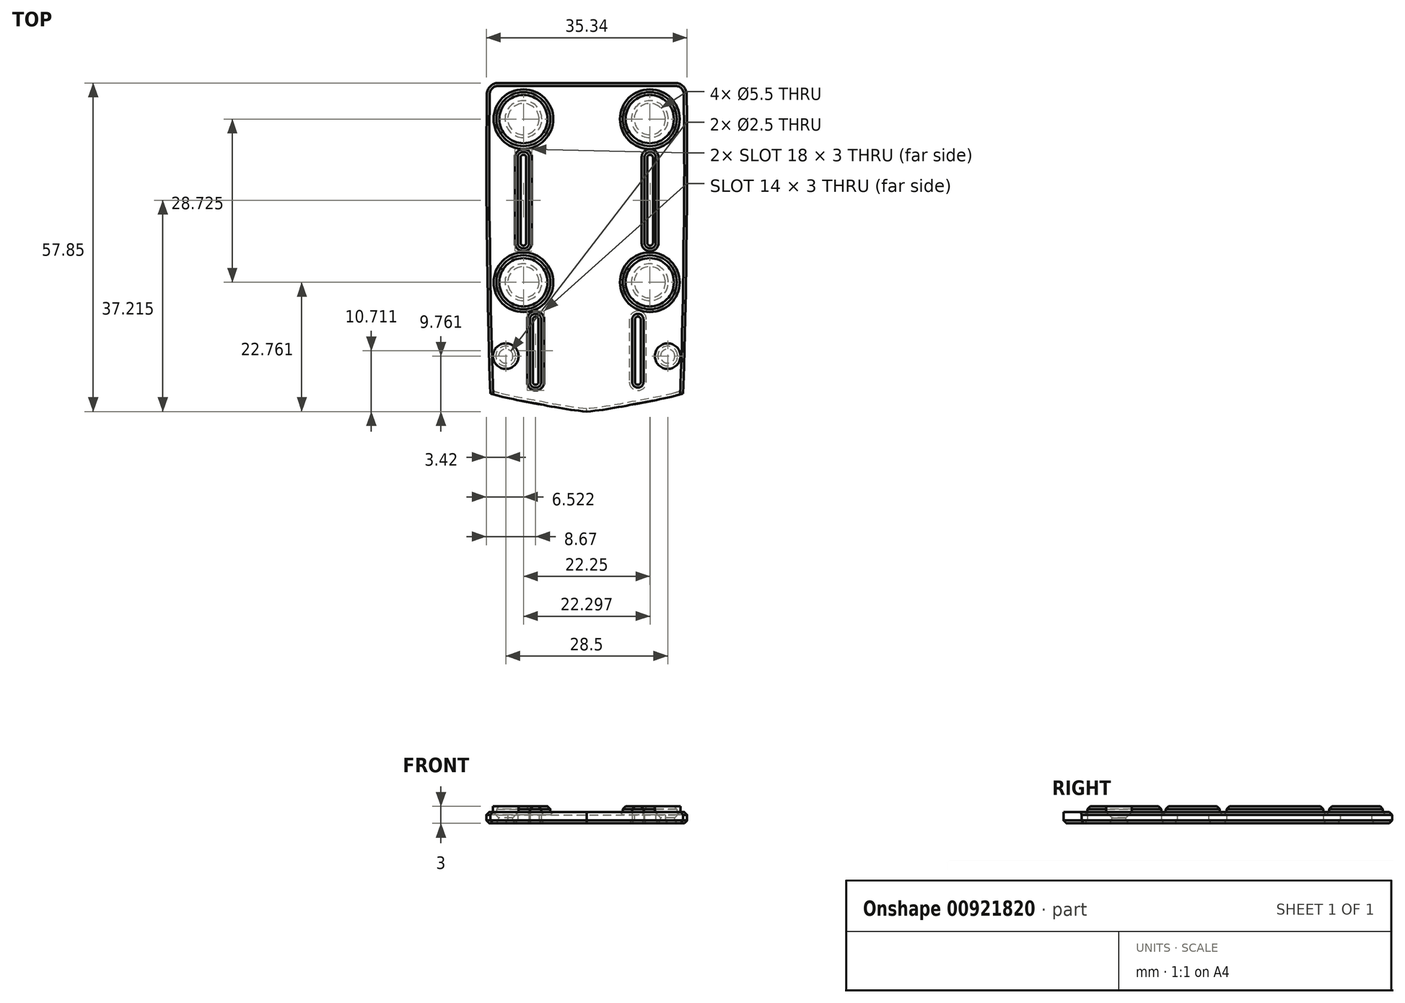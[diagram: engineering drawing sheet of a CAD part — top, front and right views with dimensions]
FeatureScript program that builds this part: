
annotation { "Feature Type Name" : "Feature", "Feature Type Description" : "" }
export const myFeature = defineFeature(function(context is Context, id is Id, definition is map)
    precondition{}
    {
        {
            var Q0;
            Q0=qCreatedBy(makeId("Top.planeOp"),FACE);
            var sketch = newSketch(context, id + "F0", { "sketchPlane" : qUnion([Q0])});
            skLineSegment(sketch, "E0", {"start": v(15.58, 12.76) * mm, "end": v(-15.58, 12.76) * mm});
            skFitSpline(sketch, "E1", {"points": [v(-17.55, 12.76) * mm, v(-17.55, -14.92) * mm, v(-16.97, -41.9) * mm], "startDerivative": vector(-1.27, -105.06) * mm, "endDerivative": vector(2.95, -84.29) * mm});
            skCircle(sketch, "E2", {"center": v(-11.15, -22.33) * mm, "radius": 2.75 * mm});
            skCircle(sketch, "E3", {"center": v(-11.15, 6.4) * mm, "radius": 2.75 * mm});
            skCircle(sketch, "E4", {"center": v(11.1, 6.4) * mm, "radius": 2.75 * mm});
            skCircle(sketch, "E5", {"center": v(11.1, -22.33) * mm, "radius": 2.75 * mm});
            skLineSegment(sketch, "E6", {"start": v(11.1, -22.33) * mm, "end": v(-19.49, -22.33) * mm, "construction": true});
            skLineSegment(sketch, "E7", {"start": v(11.1, 6.4) * mm, "end": v(-16.85, 6.4) * mm, "construction": true});
            skPoint(sketch, "E8.middle", {"position": v(0, -7.88) * mm});
            skPoint(sketch, "E9.visualSharp", {"position": v(-5, 6) * mm});
            skPoint(sketch, "E10.visualSharp", {"position": v(5, 6) * mm});
            skPoint(sketch, "E11.visualSharp", {"position": v(5, -21.75) * mm});
            skPoint(sketch, "E12.visualSharp", {"position": v(-5, -21.75) * mm});
            skFitSpline(sketch, "E13.MirrorCS", {"points": [v(17.55, 12.76) * mm, v(17.55, -14.92) * mm, v(16.97, -41.9) * mm], "startDerivative": vector(1.27, -105.06) * mm, "endDerivative": vector(-2.95, -84.29) * mm});
            skFitSpline(sketch, "E14", {"points": [v(-16.97, -41.9) * mm, v(-8.8, -43.7) * mm, v(0, -45.09) * mm], "startDerivative": vector(16.14, -4.96) * mm, "endDerivative": vector(18.25, -1.39) * mm});
            skFitSpline(sketch, "E15.MirrorCS", {"points": [v(16.97, -41.9) * mm, v(8.8, -43.7) * mm, v(0, -45.09) * mm], "startDerivative": vector(-16.14, -4.96) * mm, "endDerivative": vector(-18.25, -1.39) * mm});
            skLineSegment(sketch, "E16.left", {"start": v(-12.15, -0.37) * mm, "end": v(-12.15, -15.37) * mm});
            skLineSegment(sketch, "E16.right", {"start": v(-10.15, -0.37) * mm, "end": v(-10.15, -15.37) * mm});
            skArc(sketch, "E17", {"start": v(-12.15, -0.37) * mm, "mid": v(-11.15, 0.63) * mm, "end": v(-10.15, -0.37) * mm});
            skArc(sketch, "E18", {"start": v(-10.15, -15.37) * mm, "mid": v(-11.15, -16.37) * mm, "end": v(-12.15, -15.37) * mm});
            skLineSegment(sketch, "E19", {"start": v(-12.15, -0.37) * mm, "end": v(-10.15, -0.37) * mm, "construction": true});
            skLineSegment(sketch, "E20.MirrorCS", {"start": v(10.15, -0.37) * mm, "end": v(10.15, -15.38) * mm});
            skArc(sketch, "E21.MirrorCS", {"start": v(12.15, -0.37) * mm, "mid": v(11.15, 0.63) * mm, "end": v(10.15, -0.37) * mm});
            skLineSegment(sketch, "E22.MirrorCS", {"start": v(12.15, -0.37) * mm, "end": v(12.15, -15.37) * mm});
            skArc(sketch, "E23.MirrorCS", {"start": v(10.15, -15.38) * mm, "mid": v(11.15, -16.37) * mm, "end": v(12.15, -15.37) * mm});
            skPoint(sketch, "E24.visualSharp", {"position": v(-5, -27.63) * mm});
            skPoint(sketch, "E25.visualSharp", {"position": v(5, -41.13) * mm});
            skPoint(sketch, "E26.visualSharp", {"position": v(-5, -41.13) * mm});
            skLineSegment(sketch, "E27", {"start": v(-10, -28.88) * mm, "end": v(-10, -39.88) * mm});
            skLineSegment(sketch, "E28", {"start": v(-8, -28.88) * mm, "end": v(-8, -39.88) * mm});
            skLineSegment(sketch, "E29", {"start": v(-10, -28.88) * mm, "end": v(-8, -28.88) * mm, "construction": true});
            skArc(sketch, "E30", {"start": v(-10, -28.88) * mm, "mid": v(-9, -27.88) * mm, "end": v(-8, -28.88) * mm});
            skArc(sketch, "E31", {"start": v(-10, -39.88) * mm, "mid": v(-9, -40.88) * mm, "end": v(-8, -39.88) * mm});
            skLineSegment(sketch, "E32.MirrorCS", {"start": v(8, -28.88) * mm, "end": v(8, -39.88) * mm});
            skArc(sketch, "E33.MirrorCS", {"start": v(10, -28.88) * mm, "mid": v(9, -27.88) * mm, "end": v(8, -28.88) * mm});
            skLineSegment(sketch, "E34.MirrorCS", {"start": v(10, -28.88) * mm, "end": v(10, -39.88) * mm});
            skArc(sketch, "E35.MirrorCS", {"start": v(10, -39.88) * mm, "mid": v(9, -40.88) * mm, "end": v(8, -39.88) * mm});
            skLineSegment(sketch, "E36", {"start": v(11.1, 6.4) * mm, "end": v(11.1, -23.42) * mm, "construction": true});
            skLineSegment(sketch, "E37", {"start": v(-5, -7.87) * mm, "end": v(-10.15, -7.87) * mm, "construction": true});
            skLineSegment(sketch, "E38", {"start": v(-5, -34.38) * mm, "end": v(-8, -34.38) * mm, "construction": true});
            skArc(sketch, "E39.filletArc", {"start": v(-15.58, 12.76) * mm, "mid": v(-16.98, 12.18) * mm, "end": v(-17.58, 10.78) * mm});
            skArc(sketch, "E40.filletArc", {"start": v(17.58, 10.78) * mm, "mid": v(16.98, 12.18) * mm, "end": v(15.58, 12.76) * mm});
            skArc(sketch, "E41.filletArc", {"start": v(15.52, -42.31) * mm, "mid": v(16.58, -41.63) * mm, "end": v(17.02, -40.45) * mm});
            skArc(sketch, "E42.filletArc", {"start": v(-17.02, -40.45) * mm, "mid": v(-16.58, -41.63) * mm, "end": v(-15.52, -42.31) * mm});
            skCircle(sketch, "E43.0", {"center": v(-11.15, -22.33) * mm, "radius": 4.75 * mm});
            skCircle(sketch, "E44.0", {"center": v(11.1, -22.33) * mm, "radius": 4.75 * mm});
            skCircle(sketch, "E45.0", {"center": v(-11.15, 6.4) * mm, "radius": 4.75 * mm});
            skCircle(sketch, "E46.0", {"center": v(11.1, 6.4) * mm, "radius": 4.75 * mm});
            skLineSegment(sketch, "E47", {"start": v(-14.25, -35.33) * mm, "end": v(14.25, -35.33) * mm, "construction": true});
            skLineSegment(sketch, "E48", {"start": v(-11.15, -22.33) * mm, "end": v(-11.15, -15.37) * mm, "construction": true});
            skSolve(sketch);
        }
        {
            var Q0;
            Q0 = qSketchRegion(id + "F0", true);
            extrude(context, id + "F1", {"entities" : qUnion([Q0]), "depth" : 2 * mm, "offsetDistance" : 25 * mm});
        }
        {
            var Q0;
            Q0=makeQuery(id+"F0.imprint","IMPRINT",FACE,{"disambiguationData":[TD([[makeQuery(id+"F0.imprint","IMPRINT",EDGE,{"derivedFrom":sQuery(id+"F0.wireOp",EDGE,"E3")}),-1.0]])]});
            var Q1;
            Q1=makeQuery(id+"F0.imprint","IMPRINT",FACE,{"disambiguationData":[TD([[makeQuery(id+"F0.imprint","IMPRINT",EDGE,{"derivedFrom":sQuery(id+"F0.wireOp",EDGE,"E4")}),-1.0]])]});
            var Q2;
            Q2=makeQuery(id+"F0.imprint","IMPRINT",FACE,{"disambiguationData":[TD([[makeQuery(id+"F0.imprint","IMPRINT",EDGE,{"derivedFrom":sQuery(id+"F0.wireOp",EDGE,"E2")}),-1.0]])]});
            var Q3;
            Q3=makeQuery(id+"F0.imprint","IMPRINT",FACE,{"disambiguationData":[TD([[makeQuery(id+"F0.imprint","IMPRINT",EDGE,{"derivedFrom":sQuery(id+"F0.wireOp",EDGE,"E5")}),-1.0]])]});
            extrude(context, id + "F2", {"entities" : qUnion([Q0, Q1, Q2, Q3]), "operationType" : NewBodyOperationType.ADD, "depth" : 1.5 * mm, "offsetDistance" : 25 * mm});
        }
        {
            var Q0;
            Q0=makeQuery(id+"F1.opExtrude","CAP_FACE",FACE,{"disambiguationData":[OSD([sQuery(id+"F0.wireOp",EDGE,"E0"),sQuery(id+"F0.wireOp",EDGE,"E1"),sQuery(id+"F0.wireOp",EDGE,"E8.bottom"),sQuery(id+"F0.wireOp",EDGE,"E8.top"),sQuery(id+"F0.wireOp",EDGE,"E8.left"),sQuery(id+"F0.wireOp",EDGE,"E8.right"),sQuery(id+"F0.wireOp",EDGE,"E9.filletArc"),sQuery(id+"F0.wireOp",EDGE,"E10.filletArc"),sQuery(id+"F0.wireOp",EDGE,"E11.filletArc"),sQuery(id+"F0.wireOp",EDGE,"E12.filletArc"),sQuery(id+"F0.wireOp",EDGE,"E13.MirrorCS"),sQuery(id+"F0.wireOp",EDGE,"E14"),sQuery(id+"F0.wireOp",EDGE,"E15.MirrorCS"),sQuery(id+"F0.wireOp",EDGE,"E16.left"),sQuery(id+"F0.wireOp",EDGE,"E16.right"),sQuery(id+"F0.wireOp",EDGE,"E17"),sQuery(id+"F0.wireOp",EDGE,"E18"),sQuery(id+"F0.wireOp",EDGE,"E20.MirrorCS"),sQuery(id+"F0.wireOp",EDGE,"E21.MirrorCS"),sQuery(id+"F0.wireOp",EDGE,"E22.MirrorCS"),sQuery(id+"F0.wireOp",EDGE,"E23.MirrorCS"),sQuery(id+"F0.wireOp",EDGE,"LDVhsGNf-NW9R-3dpW-trcF-fsA8RbAyW16g.bottom"),sQuery(id+"F0.wireOp",EDGE,"LDVhsGNf-NW9R-3dpW-trcF-fsA8RbAyW16g.top"),sQuery(id+"F0.wireOp",EDGE,"LDVhsGNf-NW9R-3dpW-trcF-fsA8RbAyW16g.left"),sQuery(id+"F0.wireOp",EDGE,"LDVhsGNf-NW9R-3dpW-trcF-fsA8RbAyW16g.right"),sQuery(id+"F0.wireOp",EDGE,"E24.filletArc"),sQuery(id+"F0.wireOp",EDGE,"f2ea6e7a-d335-4226-a1ad-7d290ac42285.filletArc"),sQuery(id+"F0.wireOp",EDGE,"E25.filletArc"),sQuery(id+"F0.wireOp",EDGE,"E26.filletArc"),sQuery(id+"F0.wireOp",EDGE,"E27"),sQuery(id+"F0.wireOp",EDGE,"E28"),sQuery(id+"F0.wireOp",EDGE,"E30"),sQuery(id+"F0.wireOp",EDGE,"E31"),sQuery(id+"F0.wireOp",EDGE,"E32.MirrorCS"),sQuery(id+"F0.wireOp",EDGE,"E33.MirrorCS"),sQuery(id+"F0.wireOp",EDGE,"E34.MirrorCS"),sQuery(id+"F0.wireOp",EDGE,"E35.MirrorCS"),sQuery(id+"F0.wireOp",EDGE,"E39.filletArc"),sQuery(id+"F0.wireOp",EDGE,"E40.filletArc"),sQuery(id+"F0.wireOp",EDGE,"E41.filletArc"),sQuery(id+"F0.wireOp",EDGE,"E42.filletArc"),sQuery(id+"F0.wireOp",EDGE,"E43.0"),sQuery(id+"F0.wireOp",EDGE,"E44.0"),sQuery(id+"F0.wireOp",EDGE,"E45.0"),sQuery(id+"F0.wireOp",EDGE,"E46.0")])],"isStart":false});
            var sketch = newSketch(context, id + "F3", { "sketchPlane" : qUnion([Q0])});
            skPoint(sketch, "E49.0", {"position": v(-14.25, -35.33) * mm});
            skPoint(sketch, "E50.0", {"position": v(14.25, -35.33) * mm});
            skSolve(sketch);
        }
        {
            var Q0;
            Q0=sQuery(id+"F3.wireOp",VERTEX,"E49.0");
            var Q1;
            Q1=sQuery(id+"F3.wireOp",VERTEX,"E50.0");
            var Q2;
            Q2=makeQuery(id+"F1.opExtrude","SWEPT_BODY",BODY,{"disambiguationData":[OSD([sQuery(id+"F0.wireOp",EDGE,"E0"),sQuery(id+"F0.wireOp",EDGE,"E1"),sQuery(id+"F0.wireOp",EDGE,"E8.bottom"),sQuery(id+"F0.wireOp",EDGE,"E8.top"),sQuery(id+"F0.wireOp",EDGE,"E8.left"),sQuery(id+"F0.wireOp",EDGE,"E8.right"),sQuery(id+"F0.wireOp",EDGE,"E9.filletArc"),sQuery(id+"F0.wireOp",EDGE,"E10.filletArc"),sQuery(id+"F0.wireOp",EDGE,"E11.filletArc"),sQuery(id+"F0.wireOp",EDGE,"E12.filletArc"),sQuery(id+"F0.wireOp",EDGE,"E13.MirrorCS"),sQuery(id+"F0.wireOp",EDGE,"E14"),sQuery(id+"F0.wireOp",EDGE,"E15.MirrorCS"),sQuery(id+"F0.wireOp",EDGE,"E16.left"),sQuery(id+"F0.wireOp",EDGE,"E16.right"),sQuery(id+"F0.wireOp",EDGE,"E17"),sQuery(id+"F0.wireOp",EDGE,"E18"),sQuery(id+"F0.wireOp",EDGE,"E20.MirrorCS"),sQuery(id+"F0.wireOp",EDGE,"E21.MirrorCS"),sQuery(id+"F0.wireOp",EDGE,"E22.MirrorCS"),sQuery(id+"F0.wireOp",EDGE,"E23.MirrorCS"),sQuery(id+"F0.wireOp",EDGE,"LDVhsGNf-NW9R-3dpW-trcF-fsA8RbAyW16g.bottom"),sQuery(id+"F0.wireOp",EDGE,"LDVhsGNf-NW9R-3dpW-trcF-fsA8RbAyW16g.top"),sQuery(id+"F0.wireOp",EDGE,"LDVhsGNf-NW9R-3dpW-trcF-fsA8RbAyW16g.left"),sQuery(id+"F0.wireOp",EDGE,"LDVhsGNf-NW9R-3dpW-trcF-fsA8RbAyW16g.right"),sQuery(id+"F0.wireOp",EDGE,"E24.filletArc"),sQuery(id+"F0.wireOp",EDGE,"f2ea6e7a-d335-4226-a1ad-7d290ac42285.filletArc"),sQuery(id+"F0.wireOp",EDGE,"E25.filletArc"),sQuery(id+"F0.wireOp",EDGE,"E26.filletArc"),sQuery(id+"F0.wireOp",EDGE,"E27"),sQuery(id+"F0.wireOp",EDGE,"E28"),sQuery(id+"F0.wireOp",EDGE,"E30"),sQuery(id+"F0.wireOp",EDGE,"E31"),sQuery(id+"F0.wireOp",EDGE,"E32.MirrorCS"),sQuery(id+"F0.wireOp",EDGE,"E33.MirrorCS"),sQuery(id+"F0.wireOp",EDGE,"E34.MirrorCS"),sQuery(id+"F0.wireOp",EDGE,"E35.MirrorCS"),sQuery(id+"F0.wireOp",EDGE,"E39.filletArc"),sQuery(id+"F0.wireOp",EDGE,"E40.filletArc"),sQuery(id+"F0.wireOp",EDGE,"E41.filletArc"),sQuery(id+"F0.wireOp",EDGE,"E42.filletArc"),sQuery(id+"F0.wireOp",EDGE,"E43.0"),sQuery(id+"F0.wireOp",EDGE,"E44.0"),sQuery(id+"F0.wireOp",EDGE,"E45.0"),sQuery(id+"F0.wireOp",EDGE,"E46.0")])]});
            hole(context, id + "F4", {"style" : HoleStyle.C_SINK, "endStyle" : HoleEndStyle.THROUGH, "holeDiameter" : 2.5 * mm, "cSinkDiameter" : 4.5 * mm, "cSinkAngle" : 90 * degree, "majorDiameter" : 5 * mm, "isTappedThrough" : true, "tappedDepth" : 12 * mm, "tapClearance" : 3, "locations" : qUnion([Q0, Q1]), "scope" : qUnion([Q2])});
        }
        {
            var Q0;
            Q0=makeQuery(id+"F1.opExtrude","CAP_FACE",FACE,{"disambiguationData":[OSD([sQuery(id+"F0.wireOp",EDGE,"E0"),sQuery(id+"F0.wireOp",EDGE,"E1"),sQuery(id+"F0.wireOp",EDGE,"E13.MirrorCS"),sQuery(id+"F0.wireOp",EDGE,"E14"),sQuery(id+"F0.wireOp",EDGE,"E15.MirrorCS"),sQuery(id+"F0.wireOp",EDGE,"E16.left"),sQuery(id+"F0.wireOp",EDGE,"E16.right"),sQuery(id+"F0.wireOp",EDGE,"E17"),sQuery(id+"F0.wireOp",EDGE,"E18"),sQuery(id+"F0.wireOp",EDGE,"E20.MirrorCS"),sQuery(id+"F0.wireOp",EDGE,"E21.MirrorCS"),sQuery(id+"F0.wireOp",EDGE,"E22.MirrorCS"),sQuery(id+"F0.wireOp",EDGE,"E23.MirrorCS"),sQuery(id+"F0.wireOp",EDGE,"E27"),sQuery(id+"F0.wireOp",EDGE,"E28"),sQuery(id+"F0.wireOp",EDGE,"E30"),sQuery(id+"F0.wireOp",EDGE,"E31"),sQuery(id+"F0.wireOp",EDGE,"E32.MirrorCS"),sQuery(id+"F0.wireOp",EDGE,"E33.MirrorCS"),sQuery(id+"F0.wireOp",EDGE,"E34.MirrorCS"),sQuery(id+"F0.wireOp",EDGE,"E35.MirrorCS"),sQuery(id+"F0.wireOp",EDGE,"E39.filletArc"),sQuery(id+"F0.wireOp",EDGE,"E40.filletArc"),sQuery(id+"F0.wireOp",EDGE,"E41.filletArc"),sQuery(id+"F0.wireOp",EDGE,"E42.filletArc"),sQuery(id+"F0.wireOp",EDGE,"E43.0"),sQuery(id+"F0.wireOp",EDGE,"E44.0"),sQuery(id+"F0.wireOp",EDGE,"E45.0"),sQuery(id+"F0.wireOp",EDGE,"E46.0")])],"isStart":false});
            var sketch = newSketch(context, id + "F5", { "sketchPlane" : qUnion([Q0])});
            skFitSpline(sketch, "E51.0.0", {"points": [v(0, -45.09) * mm, v(3.09, -44.85) * mm, v(8.72, -43.66) * mm, v(14.32, -42.72) * mm, v(16.97, -41.9) * mm]});
            skArc(sketch, "E51.0.1", {"start": v(15.52, -42.31) * mm, "mid": v(16.58, -41.63) * mm, "end": v(17.02, -40.45) * mm});
            skFitSpline(sketch, "E51.0.2", {"points": [v(16.97, -41.9) * mm, v(17.45, -27.95) * mm, v(17.5, -13.3) * mm, v(17.77, -4.86) * mm, v(17.55, 12.76) * mm]});
            skArc(sketch, "E51.0.3", {"start": v(17.58, 10.78) * mm, "mid": v(16.98, 12.18) * mm, "end": v(15.58, 12.76) * mm});
            skLineSegment(sketch, "E51.0.4", {"start": v(15.58, 12.76) * mm, "end": v(-15.58, 12.76) * mm});
            skArc(sketch, "E51.0.5", {"start": v(-15.58, 12.76) * mm, "mid": v(-16.98, 12.18) * mm, "end": v(-17.58, 10.78) * mm});
            skFitSpline(sketch, "E51.0.6", {"points": [v(-17.55, 12.76) * mm, v(-17.77, -4.86) * mm, v(-17.5, -13.3) * mm, v(-17.45, -27.95) * mm, v(-16.97, -41.9) * mm]});
            skArc(sketch, "E51.0.7", {"start": v(-17.02, -40.45) * mm, "mid": v(-16.58, -41.63) * mm, "end": v(-15.52, -42.31) * mm});
            skFitSpline(sketch, "E51.0.8", {"points": [v(-16.97, -41.9) * mm, v(-14.32, -42.72) * mm, v(-8.72, -43.66) * mm, v(-3.09, -44.85) * mm, v(0, -45.09) * mm]});
            skCircle(sketch, "E52.0", {"center": v(-14.25, -35.33) * mm, "radius": 2.25 * mm});
            skCircle(sketch, "E53.0", {"center": v(-11.15, -22.33) * mm, "radius": 4.75 * mm});
            skCircle(sketch, "E54.0", {"center": v(-11.15, 6.4) * mm, "radius": 4.75 * mm});
            skCircle(sketch, "E55.0", {"center": v(11.1, 6.4) * mm, "radius": 4.75 * mm});
            skCircle(sketch, "E56.0", {"center": v(11.1, -22.33) * mm, "radius": 4.75 * mm});
            skLineSegment(sketch, "E57.0", {"start": v(10.15, -0.37) * mm, "end": v(10.15, -15.38) * mm});
            skArc(sketch, "E58.0", {"start": v(10.15, -15.38) * mm, "mid": v(11.15, -16.37) * mm, "end": v(12.15, -15.37) * mm});
            skLineSegment(sketch, "E59.0", {"start": v(12.15, -0.37) * mm, "end": v(12.15, -15.37) * mm});
            skArc(sketch, "E60.0", {"start": v(12.15, -0.37) * mm, "mid": v(11.15, 0.63) * mm, "end": v(10.15, -0.37) * mm});
            skLineSegment(sketch, "E61.0", {"start": v(10, -28.88) * mm, "end": v(10, -39.88) * mm});
            skArc(sketch, "E62.0", {"start": v(10, -28.88) * mm, "mid": v(9, -27.88) * mm, "end": v(8, -28.88) * mm});
            skLineSegment(sketch, "E63.0", {"start": v(8, -28.88) * mm, "end": v(8, -39.88) * mm});
            skArc(sketch, "E64.0", {"start": v(10, -39.88) * mm, "mid": v(9, -40.88) * mm, "end": v(8, -39.88) * mm});
            skCircle(sketch, "E65.0", {"center": v(14.25, -35.33) * mm, "radius": 2.25 * mm});
            skLineSegment(sketch, "E66.0", {"start": v(-8, -28.88) * mm, "end": v(-8, -39.88) * mm});
            skLineSegment(sketch, "E67.0", {"start": v(-10, -28.88) * mm, "end": v(-10, -39.88) * mm});
            skArc(sketch, "E68.0", {"start": v(-10, -39.88) * mm, "mid": v(-9, -40.88) * mm, "end": v(-8, -39.88) * mm});
            skPoint(sketch, "E69.0", {"position": v(-9, -27.88) * mm});
            skLineSegment(sketch, "E70.0", {"start": v(-10.15, -0.37) * mm, "end": v(-10.15, -15.37) * mm});
            skPoint(sketch, "E71.0", {"position": v(-11.15, -16.37) * mm});
            skLineSegment(sketch, "E72.0", {"start": v(-12.15, -0.37) * mm, "end": v(-12.15, -15.37) * mm});
            skArc(sketch, "E73.0", {"start": v(-10.15, -15.37) * mm, "mid": v(-11.15, -16.37) * mm, "end": v(-12.15, -15.37) * mm});
            skArc(sketch, "E74.0", {"start": v(-12.15, -0.37) * mm, "mid": v(-11.15, 0.63) * mm, "end": v(-10.15, -0.37) * mm});
            skArc(sketch, "E75.0", {"start": v(-10, -28.88) * mm, "mid": v(-9, -27.88) * mm, "end": v(-8, -28.88) * mm});
            skSolve(sketch);
        }
        {
            var Q0;
            Q0 = qSketchRegion(id + "F5", true);
            extrude(context, id + "F6", {"entities" : qUnion([Q0]), "operationType" : NewBodyOperationType.ADD, "depth" : 1 * mm, "offsetDistance" : 25 * mm});
        }
        {
            var Q0;
            {var subQ0=sQuery(id+"F0.wireOp",EDGE,"E44.0");var subQ1=sQuery(id+"F0.wireOp",EDGE,"E46.0");var subQ2=sQuery(id+"F0.wireOp",EDGE,"E45.0");var subQ3=sQuery(id+"F0.wireOp",EDGE,"E43.0");Q0=makeQuery(id+"F2.boolean.opBoolean","MERGE",FACE,{"derivedFrom":[makeQuery(id+"F1.opExtrude","CAP_FACE",FACE,{"disambiguationData":[OSD([sQuery(id+"F0.wireOp",EDGE,"E0"),sQuery(id+"F0.wireOp",EDGE,"E1"),sQuery(id+"F0.wireOp",EDGE,"E8.bottom"),sQuery(id+"F0.wireOp",EDGE,"E8.top"),sQuery(id+"F0.wireOp",EDGE,"E8.left"),sQuery(id+"F0.wireOp",EDGE,"E8.right"),sQuery(id+"F0.wireOp",EDGE,"E9.filletArc"),sQuery(id+"F0.wireOp",EDGE,"E10.filletArc"),sQuery(id+"F0.wireOp",EDGE,"E11.filletArc"),sQuery(id+"F0.wireOp",EDGE,"E12.filletArc"),sQuery(id+"F0.wireOp",EDGE,"E13.MirrorCS"),sQuery(id+"F0.wireOp",EDGE,"E14"),sQuery(id+"F0.wireOp",EDGE,"E15.MirrorCS"),sQuery(id+"F0.wireOp",EDGE,"E16.left"),sQuery(id+"F0.wireOp",EDGE,"E16.right"),sQuery(id+"F0.wireOp",EDGE,"E17"),sQuery(id+"F0.wireOp",EDGE,"E18"),sQuery(id+"F0.wireOp",EDGE,"E20.MirrorCS"),sQuery(id+"F0.wireOp",EDGE,"E21.MirrorCS"),sQuery(id+"F0.wireOp",EDGE,"E22.MirrorCS"),sQuery(id+"F0.wireOp",EDGE,"E23.MirrorCS"),sQuery(id+"F0.wireOp",EDGE,"LDVhsGNf-NW9R-3dpW-trcF-fsA8RbAyW16g.bottom"),sQuery(id+"F0.wireOp",EDGE,"LDVhsGNf-NW9R-3dpW-trcF-fsA8RbAyW16g.top"),sQuery(id+"F0.wireOp",EDGE,"LDVhsGNf-NW9R-3dpW-trcF-fsA8RbAyW16g.left"),sQuery(id+"F0.wireOp",EDGE,"LDVhsGNf-NW9R-3dpW-trcF-fsA8RbAyW16g.right"),sQuery(id+"F0.wireOp",EDGE,"E24.filletArc"),sQuery(id+"F0.wireOp",EDGE,"f2ea6e7a-d335-4226-a1ad-7d290ac42285.filletArc"),sQuery(id+"F0.wireOp",EDGE,"E25.filletArc"),sQuery(id+"F0.wireOp",EDGE,"E26.filletArc"),sQuery(id+"F0.wireOp",EDGE,"E27"),sQuery(id+"F0.wireOp",EDGE,"E28"),sQuery(id+"F0.wireOp",EDGE,"E30"),sQuery(id+"F0.wireOp",EDGE,"E31"),sQuery(id+"F0.wireOp",EDGE,"E32.MirrorCS"),sQuery(id+"F0.wireOp",EDGE,"E33.MirrorCS"),sQuery(id+"F0.wireOp",EDGE,"E34.MirrorCS"),sQuery(id+"F0.wireOp",EDGE,"E35.MirrorCS"),sQuery(id+"F0.wireOp",EDGE,"E39.filletArc"),sQuery(id+"F0.wireOp",EDGE,"E40.filletArc"),sQuery(id+"F0.wireOp",EDGE,"E41.filletArc"),sQuery(id+"F0.wireOp",EDGE,"E42.filletArc"),subQ3,subQ0,subQ2,subQ1])],"isStart":true}),makeQuery(id+"F2.opExtrude","CAP_FACE",FACE,{"disambiguationData":[OSD([sQuery(id+"F0.wireOp",EDGE,"E2"),subQ3])],"isStart":true}),makeQuery(id+"F2.opExtrude","CAP_FACE",FACE,{"disambiguationData":[OSD([sQuery(id+"F0.wireOp",EDGE,"E3"),subQ2])],"isStart":true}),makeQuery(id+"F2.opExtrude","CAP_FACE",FACE,{"disambiguationData":[OSD([sQuery(id+"F0.wireOp",EDGE,"E4"),subQ1])],"isStart":true}),makeQuery(id+"F2.opExtrude","CAP_FACE",FACE,{"disambiguationData":[OSD([sQuery(id+"F0.wireOp",EDGE,"E5"),subQ0])],"isStart":true})]});}
            var Q1;
            Q1=makeQuery(id+"F1.opExtrude","CAP_EDGE",EDGE,{"disambiguationData":[OSD([sQuery(id+"F0.wireOp",EDGE,"E1")])],"isStart":false});
            var Q2;
            Q2=makeQuery(id+"F1.opExtrude","CAP_EDGE",EDGE,{"disambiguationData":[OSD([sQuery(id+"F0.wireOp",EDGE,"E27")])],"isStart":false});
            var Q3;
            Q3=makeQuery(id+"F1.opExtrude","CAP_EDGE",EDGE,{"disambiguationData":[OSD([sQuery(id+"F0.wireOp",EDGE,"LDVhsGNf-NW9R-3dpW-trcF-fsA8RbAyW16g.left")])],"isStart":false});
            var Q4;
            Q4=makeQuery(id+"F1.opExtrude","CAP_EDGE",EDGE,{"disambiguationData":[OSD([sQuery(id+"F0.wireOp",EDGE,"E8.left")])],"isStart":false});
            var Q5;
            Q5=makeQuery(id+"F1.opExtrude","CAP_EDGE",EDGE,{"disambiguationData":[OSD([sQuery(id+"F0.wireOp",EDGE,"E16.right")])],"isStart":false});
            var Q6;
            Q6=makeQuery(id+"F1.opExtrude","CAP_EDGE",EDGE,{"disambiguationData":[OSD([sQuery(id+"F0.wireOp",EDGE,"E43.0")])],"isStart":false});
            var Q7;
            Q7=makeQuery(id+"F1.opExtrude","CAP_EDGE",EDGE,{"disambiguationData":[OSD([sQuery(id+"F0.wireOp",EDGE,"E44.0")])],"isStart":false});
            var Q8;
            Q8=makeQuery(id+"F1.opExtrude","CAP_EDGE",EDGE,{"disambiguationData":[OSD([sQuery(id+"F0.wireOp",EDGE,"E46.0")])],"isStart":false});
            var Q9;
            Q9=makeQuery(id+"F1.opExtrude","CAP_EDGE",EDGE,{"disambiguationData":[OSD([sQuery(id+"F0.wireOp",EDGE,"E20.MirrorCS")])],"isStart":false});
            var Q10;
            Q10=makeQuery(id+"F1.opExtrude","CAP_EDGE",EDGE,{"disambiguationData":[OSD([sQuery(id+"F0.wireOp",EDGE,"E45.0")])],"isStart":false});
            var Q11;
            Q11=makeQuery(id+"F6.opExtrude","CAP_EDGE",EDGE,{"disambiguationData":[OSD([sQuery(id+"F5.wireOp",EDGE,"E51.0.6")])],"isStart":false});
            var Q12;
            Q12=makeQuery(id+"F6.opExtrude","CAP_EDGE",EDGE,{"disambiguationData":[OSD([sQuery(id+"F5.wireOp",EDGE,"E53.0")])],"isStart":false});
            var Q13;
            Q13=makeQuery(id+"F6.opExtrude","CAP_EDGE",EDGE,{"disambiguationData":[OSD([sQuery(id+"F5.wireOp",EDGE,"E54.0")])],"isStart":false});
            var Q14;
            Q14=makeQuery(id+"F6.opExtrude","CAP_EDGE",EDGE,{"disambiguationData":[OSD([sQuery(id+"F5.wireOp",EDGE,"E56.0")])],"isStart":false});
            var Q15;
            Q15=makeQuery(id+"F6.opExtrude","CAP_EDGE",EDGE,{"disambiguationData":[OSD([sQuery(id+"F5.wireOp",EDGE,"E55.0")])],"isStart":false});
            var Q16;
            Q16=makeQuery(id+"F6.opExtrude","CAP_EDGE",EDGE,{"disambiguationData":[OSD([sQuery(id+"F5.wireOp",EDGE,"E70.0")])],"isStart":false});
            var Q17;
            Q17=makeQuery(id+"F6.opExtrude","CAP_EDGE",EDGE,{"disambiguationData":[OSD([sQuery(id+"F5.wireOp",EDGE,"E57.0")])],"isStart":false});
            var Q18;
            Q18=makeQuery(id+"F6.opExtrude","CAP_EDGE",EDGE,{"disambiguationData":[OSD([sQuery(id+"F5.wireOp",EDGE,"E63.0")])],"isStart":false});
            var Q19;
            Q19=makeQuery(id+"F6.opExtrude","CAP_EDGE",EDGE,{"disambiguationData":[OSD([sQuery(id+"F5.wireOp",EDGE,"E66.0")])],"isStart":false});
            chamfer(context, id + "F7", {"entities" : qUnion([Q0, Q1, Q2, Q3, Q4, Q5, Q6, Q7, Q8, Q9, Q10, Q11, Q12, Q13, Q14, Q15, Q16, Q17, Q18, Q19]), "width" : 0.5 * mm, "tangentPropagation" : true});
        }
    });
